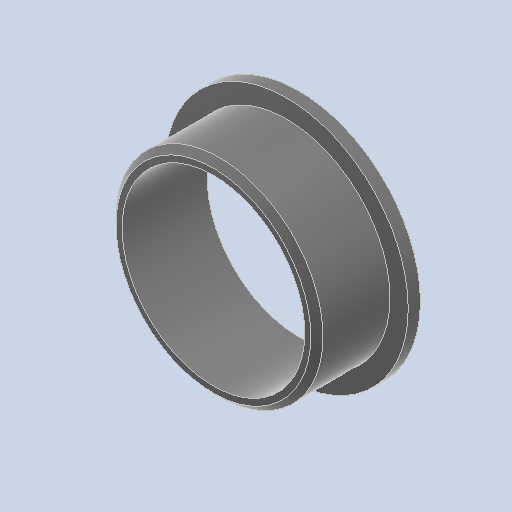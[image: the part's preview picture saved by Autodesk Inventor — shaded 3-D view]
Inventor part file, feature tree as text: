
AUTODESK INVENTOR PART (.ipt)
format: ipt  version: 2023 (Build 270158030, 158C)  size: 146,432 bytes
history: native  units: mm
features: extrude x2, sketch x2, chamfer x1
ambient origin geometry x8: Origin, YZ Plane, XZ Plane, XY Plane, X Axis, Y Axis, Z Axis, Center Point
bodies: Solid1 (feature_tree)
feature tree (5):
  extrude  "Extrusion1"  Depth=20.0mm
  extrude  "Extrusion2"  Depth=6.0mm
  chamfer  "Chamfer1"  Distance=6.0mm
  sketch  "Sketch1"  dims[d0=15.0mm d1=20.0mm]
  sketch  "Sketch2"  dims[d2=1.0mm d3=0.0mm d4=17.0mm d5=6.0mm d6=0.0mm d7=0.5mm d8=2.0mm d9=45.0deg]
